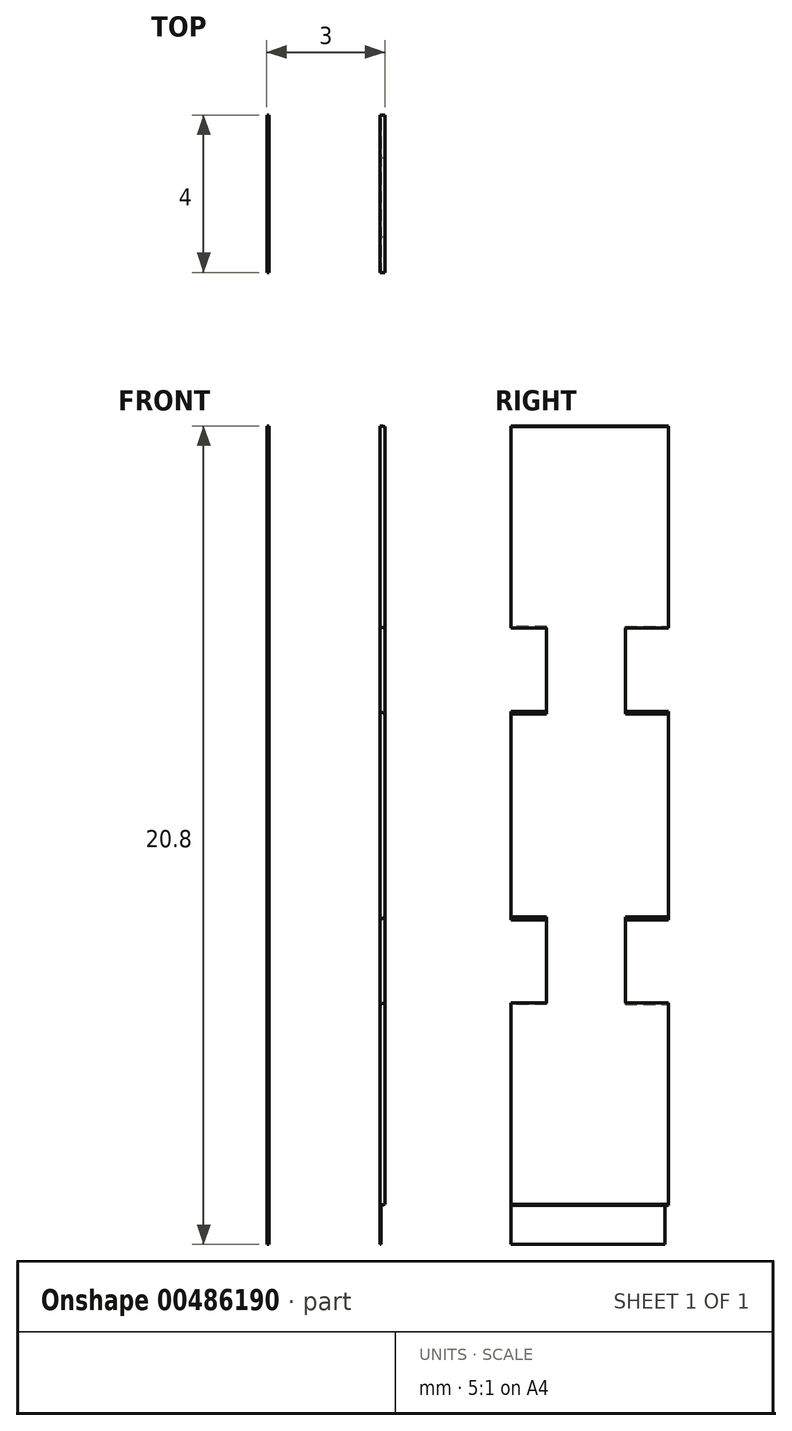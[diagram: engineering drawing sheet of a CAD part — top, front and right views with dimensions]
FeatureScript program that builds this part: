
annotation { "Feature Type Name" : "Feature", "Feature Type Description" : "" }
export const myFeature = defineFeature(function(context is Context, id is Id, definition is map)
    precondition{}
    {
        {
            var Q0;
            Q0=qCreatedBy(makeId("Front.planeOp"),FACE);
            var sketch = newSketch(context, id + "F0", { "sketchPlane" : qUnion([Q0])});
            skCircle(sketch, "E0", {"center": v(0, 0) * mm, "radius": 10 * mm});
            skSolve(sketch);
        }
        {
            var Q0;
            Q0=makeQuery(id+"F0.imprint","IMPRINT",FACE,{"disambiguationData":[TD([[makeQuery(id+"F0.imprint","IMPRINT",EDGE,{"derivedFrom":sQuery(id+"F0.wireOp",EDGE,"E0")}),1.0]])]});
            extrude(context, id + "F1", {"entities" : qUnion([Q0]), "depth" : 3.17 * mm});
        }
        {
            var Q0;
            Q0=makeQuery(id+"F0.imprint","IMPRINT",FACE,{"disambiguationData":[TD([[makeQuery(id+"F0.imprint","IMPRINT",EDGE,{"derivedFrom":sQuery(id+"F0.wireOp",EDGE,"E0")}),1.0]])]});
            extrude(context, id + "F2", {"entities" : qUnion([Q0]), "operationType" : NewBodyOperationType.ADD, "oppositeDirection" : true, "depth" : 3.17 * mm});
        }
        {
            var Q0;
            Q0=makeQuery(id+"F1.opExtrude","CAP_FACE",FACE,{"disambiguationData":[OSD([sQuery(id+"F0.wireOp",EDGE,"E0")])],"isStart":false});
            var sketch = newSketch(context, id + "F3", { "sketchPlane" : qUnion([Q0])});
            skCircle(sketch, "E1", {"center": v(0, 0) * mm, "radius": 5 * mm});
            skCircle(sketch, "E2", {"center": v(0, 0) * mm, "radius": 3 * mm});
            skSolve(sketch);
        }
        {
            var Q0;
            Q0=makeQuery(id+"F3.imprint","IMPRINT",FACE,{"disambiguationData":[TD([[makeQuery(id+"F3.imprint","IMPRINT",EDGE,{"derivedFrom":sQuery(id+"F3.wireOp",EDGE,"E1")}),1.0]])]});
            extrude(context, id + "F4", {"entities" : qUnion([Q0]), "operationType" : NewBodyOperationType.REMOVE, "oppositeDirection" : true, "depth" : 2.17 * mm});
        }
        {
            var Q0;
            Q0=makeQuery(id+"F2.opExtrude","CAP_FACE",FACE,{"disambiguationData":[OSD([sQuery(id+"F0.wireOp",EDGE,"E0")])],"isStart":false});
            var sketch = newSketch(context, id + "F5", { "sketchPlane" : qUnion([Q0])});
            skCircle(sketch, "E3", {"center": v(0, 0) * mm, "radius": 3 * mm});
            skCircle(sketch, "E4", {"center": v(0, 0) * mm, "radius": 5 * mm});
            skSolve(sketch);
        }
        {
            var Q0;
            Q0=makeQuery(id+"F5.imprint","IMPRINT",FACE,{"disambiguationData":[TD([[makeQuery(id+"F5.imprint","IMPRINT",EDGE,{"derivedFrom":sQuery(id+"F5.wireOp",EDGE,"E3")}),-1.0]])]});
            extrude(context, id + "F6", {"entities" : qUnion([Q0]), "operationType" : NewBodyOperationType.REMOVE, "oppositeDirection" : true, "depth" : 2.17 * mm});
        }
        {
            var Q0;
            Q0=qCreatedBy(makeId("Top.planeOp"),FACE);
            cPlane(context, id + "F7", {"entities" : qUnion([Q0]), "cplaneType" : CPlaneType.OFFSET, "offset" : 9.9 * mm, "oppositeDirection" : true, "width" : 150 * mm, "height" : 150 * mm});
        }
        {
            var Q0;
            Q0=qCreatedBy(id+"F7.planeOp",FACE);
            var sketch = newSketch(context, id + "F8", { "sketchPlane" : qUnion([Q0])});
            skLineSegment(sketch, "E5", {"start": v(-1.56, 2) * mm, "end": v(-0.56, 2) * mm});
            skLineSegment(sketch, "E6", {"start": v(-0.56, 2) * mm, "end": v(-0.56, 1) * mm});
            skLineSegment(sketch, "E7", {"start": v(-0.56, 1) * mm, "end": v(0.44, 1) * mm});
            skLineSegment(sketch, "E8", {"start": v(0.44, 1) * mm, "end": v(0.44, 2) * mm});
            skLineSegment(sketch, "E9", {"start": v(0.44, 2) * mm, "end": v(1.44, 2) * mm});
            skLineSegment(sketch, "E10", {"start": v(1.44, 2) * mm, "end": v(1.44, -2) * mm});
            skLineSegment(sketch, "E11", {"start": v(1.44, -2) * mm, "end": v(0.44, -2) * mm});
            skLineSegment(sketch, "E12", {"start": v(0.44, -2) * mm, "end": v(0.44, -1) * mm});
            skLineSegment(sketch, "E13", {"start": v(0.44, -1) * mm, "end": v(-0.56, -1) * mm});
            skLineSegment(sketch, "E14", {"start": v(-0.56, -1) * mm, "end": v(-0.56, -2) * mm});
            skLineSegment(sketch, "E15", {"start": v(-0.56, -2) * mm, "end": v(-1.56, -2) * mm});
            skLineSegment(sketch, "E16", {"start": v(-1.56, -2) * mm, "end": v(-1.56, 2) * mm});
            skSolve(sketch);
        }
        {
            var Q0;
            Q0=qCreatedBy(makeId("Top.planeOp"),FACE);
            cPlane(context, id + "F9", {"entities" : qUnion([Q0]), "cplaneType" : CPlaneType.OFFSET, "offset" : 9.9 * mm, "width" : 150 * mm, "height" : 150 * mm});
        }
        {
            var Q0;
            Q0=qCreatedBy(id+"F9.planeOp",FACE);
            var sketch = newSketch(context, id + "F10", { "sketchPlane" : qUnion([Q0])});
            skLineSegment(sketch, "E17", {"start": v(-1.47, 2.1) * mm, "end": v(-0.47, 2.1) * mm});
            skLineSegment(sketch, "E18", {"start": v(-0.47, 2.1) * mm, "end": v(-0.47, 1.1) * mm});
            skLineSegment(sketch, "E19", {"start": v(-0.47, 1.1) * mm, "end": v(0.53, 1.1) * mm});
            skLineSegment(sketch, "E20", {"start": v(0.53, 1.1) * mm, "end": v(0.53, 2.1) * mm});
            skLineSegment(sketch, "E21", {"start": v(0.53, 2.1) * mm, "end": v(1.53, 2.1) * mm});
            skLineSegment(sketch, "E22", {"start": v(1.53, 2.1) * mm, "end": v(1.53, -1.9) * mm});
            skLineSegment(sketch, "E23", {"start": v(1.53, -1.9) * mm, "end": v(0.53, -1.9) * mm});
            skLineSegment(sketch, "E24", {"start": v(0.53, -1.9) * mm, "end": v(0.53, -0.9) * mm});
            skLineSegment(sketch, "E25", {"start": v(0.53, -0.9) * mm, "end": v(-0.47, -0.9) * mm});
            skLineSegment(sketch, "E26", {"start": v(-0.47, -0.9) * mm, "end": v(-0.47, -1.9) * mm});
            skLineSegment(sketch, "E27", {"start": v(-0.47, -1.9) * mm, "end": v(-1.47, -1.9) * mm});
            skLineSegment(sketch, "E28", {"start": v(-1.47, -1.9) * mm, "end": v(-1.47, 2.1) * mm});
            skSolve(sketch);
        }
        {
            var Q0;
            Q0 = qSketchRegion(id + "F10", true);
            extrude(context, id + "F11", {"entities" : qUnion([Q0]), "operationType" : NewBodyOperationType.ADD, "depth" : 1 * mm, "offsetDistance" : 25 * mm});
        }
        {
            var Q0;
            Q0 = qSketchRegion(id + "F8", true);
            extrude(context, id + "F12", {"entities" : qUnion([Q0]), "operationType" : NewBodyOperationType.ADD, "oppositeDirection" : true, "depth" : 1 * mm, "offsetDistance" : 25 * mm});
        }
        {
            var Q0;
            Q0=qCreatedBy(makeId("Right.planeOp"),FACE);
            cPlane(context, id + "F13", {"entities" : qUnion([Q0]), "cplaneType" : CPlaneType.OFFSET, "offset" : 10 * mm, "width" : 150 * mm, "height" : 150 * mm});
        }
        {
            var Q0;
            Q0=qCreatedBy(id+"F13.planeOp",FACE);
            var sketch = newSketch(context, id + "F14", { "sketchPlane" : qUnion([Q0])});
            skLineSegment(sketch, "E29", {"start": v(-2.2, -1.7) * mm, "end": v(-2.2, -0.5) * mm});
            skLineSegment(sketch, "E30", {"start": v(-2.2, -0.5) * mm, "end": v(-1, -0.5) * mm});
            skLineSegment(sketch, "E31", {"start": v(-1, -0.5) * mm, "end": v(-1, 0.7) * mm});
            skLineSegment(sketch, "E32", {"start": v(-1, 0.7) * mm, "end": v(-2.2, 0.7) * mm});
            skLineSegment(sketch, "E33", {"start": v(2.2, 0.7) * mm, "end": v(1, 0.7) * mm});
            skLineSegment(sketch, "E34", {"start": v(1, 0.7) * mm, "end": v(1, -0.5) * mm});
            skLineSegment(sketch, "E35", {"start": v(1, -0.5) * mm, "end": v(2.2, -0.5) * mm});
            skLineSegment(sketch, "E36", {"start": v(2.2, -0.5) * mm, "end": v(2.2, -1.7) * mm});
            skLineSegment(sketch, "E37", {"start": v(2.2, -1.7) * mm, "end": v(-2.2, -1.7) * mm});
            skLineSegment(sketch, "E38", {"start": v(-2.2, 0.7) * mm, "end": v(-2.2, 1.9) * mm});
            skLineSegment(sketch, "E39", {"start": v(-2.2, 1.9) * mm, "end": v(2.2, 1.9) * mm});
            skLineSegment(sketch, "E40", {"start": v(2.2, 1.9) * mm, "end": v(2.2, 0.7) * mm});
            skSolve(sketch);
        }
        {
            var Q0;
            Q0 = qSketchRegion(id + "F14", true);
            extrude(context, id + "F15", {"entities" : qUnion([Q0]), "operationType" : NewBodyOperationType.REMOVE, "oppositeDirection" : true, "depth" : 1 * mm, "offsetDistance" : 25 * mm});
        }
        {
            var Q0;
            Q0=qCreatedBy(makeId("Right.planeOp"),FACE);
            cPlane(context, id + "F16", {"entities" : qUnion([Q0]), "cplaneType" : CPlaneType.OFFSET, "offset" : 10 * mm, "oppositeDirection" : true, "width" : 150 * mm, "height" : 150 * mm});
        }
        {
            var Q0;
            Q0=qCreatedBy(id+"F16.planeOp",FACE);
            var sketch = newSketch(context, id + "F17", { "sketchPlane" : qUnion([Q0])});
            skLineSegment(sketch, "E41", {"start": v(-2.2, -1.8) * mm, "end": v(-2.2, -0.6) * mm});
            skLineSegment(sketch, "E42", {"start": v(-2.2, -0.6) * mm, "end": v(-1, -0.6) * mm});
            skLineSegment(sketch, "E43", {"start": v(-1, -0.6) * mm, "end": v(-1, 0.6) * mm});
            skLineSegment(sketch, "E44", {"start": v(-1, 0.6) * mm, "end": v(-2.2, 0.6) * mm});
            skLineSegment(sketch, "E45", {"start": v(2.2, 0.6) * mm, "end": v(1, 0.6) * mm});
            skLineSegment(sketch, "E46", {"start": v(1, 0.6) * mm, "end": v(1, -0.6) * mm});
            skLineSegment(sketch, "E47", {"start": v(1, -0.6) * mm, "end": v(2.2, -0.6) * mm});
            skLineSegment(sketch, "E48", {"start": v(2.2, -0.6) * mm, "end": v(2.2, -1.8) * mm});
            skLineSegment(sketch, "E49", {"start": v(2.2, -1.8) * mm, "end": v(-2.2, -1.8) * mm});
            skLineSegment(sketch, "E50", {"start": v(-2.2, 0.6) * mm, "end": v(-2.2, 1.8) * mm});
            skLineSegment(sketch, "E51", {"start": v(-2.2, 1.8) * mm, "end": v(2.2, 1.8) * mm});
            skLineSegment(sketch, "E52", {"start": v(2.2, 1.8) * mm, "end": v(2.2, 0.6) * mm});
            skSolve(sketch);
        }
        {
            var Q0;
            Q0=makeQuery(id+"F17.imprint","IMPRINT",FACE,{"disambiguationData":[TD([[makeQuery(id+"F17.imprint","IMPRINT",EDGE,{"derivedFrom":sQuery(id+"F17.wireOp",EDGE,"E41")}),-1.0]])]});
            var Q1;
            Q1 = qConstructionFilter(qBodyType(qCreatedBy(id + "F17" ,EDGE), BodyType.WIRE), ConstructionObject.NO);
            extrude(context, id + "F18", {"entities" : qUnion([Q0]), "operationType" : NewBodyOperationType.REMOVE, "surfaceEntities" : qUnion([Q1]), "depth" : .75 * mm, "offsetDistance" : 25 * mm});
        }
        {
            var Q0;
            Q0=makeQuery(id+"F11.opExtrude","CAP_FACE",FACE,{"disambiguationData":[OSD([sQuery(id+"F10.wireOp",EDGE,"E17"),sQuery(id+"F10.wireOp",EDGE,"E18"),sQuery(id+"F10.wireOp",EDGE,"E19"),sQuery(id+"F10.wireOp",EDGE,"E20"),sQuery(id+"F10.wireOp",EDGE,"E21"),sQuery(id+"F10.wireOp",EDGE,"E22"),sQuery(id+"F10.wireOp",EDGE,"E23"),sQuery(id+"F10.wireOp",EDGE,"E24"),sQuery(id+"F10.wireOp",EDGE,"E25"),sQuery(id+"F10.wireOp",EDGE,"E26"),sQuery(id+"F10.wireOp",EDGE,"E27"),sQuery(id+"F10.wireOp",EDGE,"E28")])],"isStart":true});
            extrude(context, id + "F19", {"entities" : qUnion([Q0]), "operationType" : NewBodyOperationType.INTERSECT, "depth" : 3000 * mm, "offsetDistance" : 25 * mm});
        }
    });
